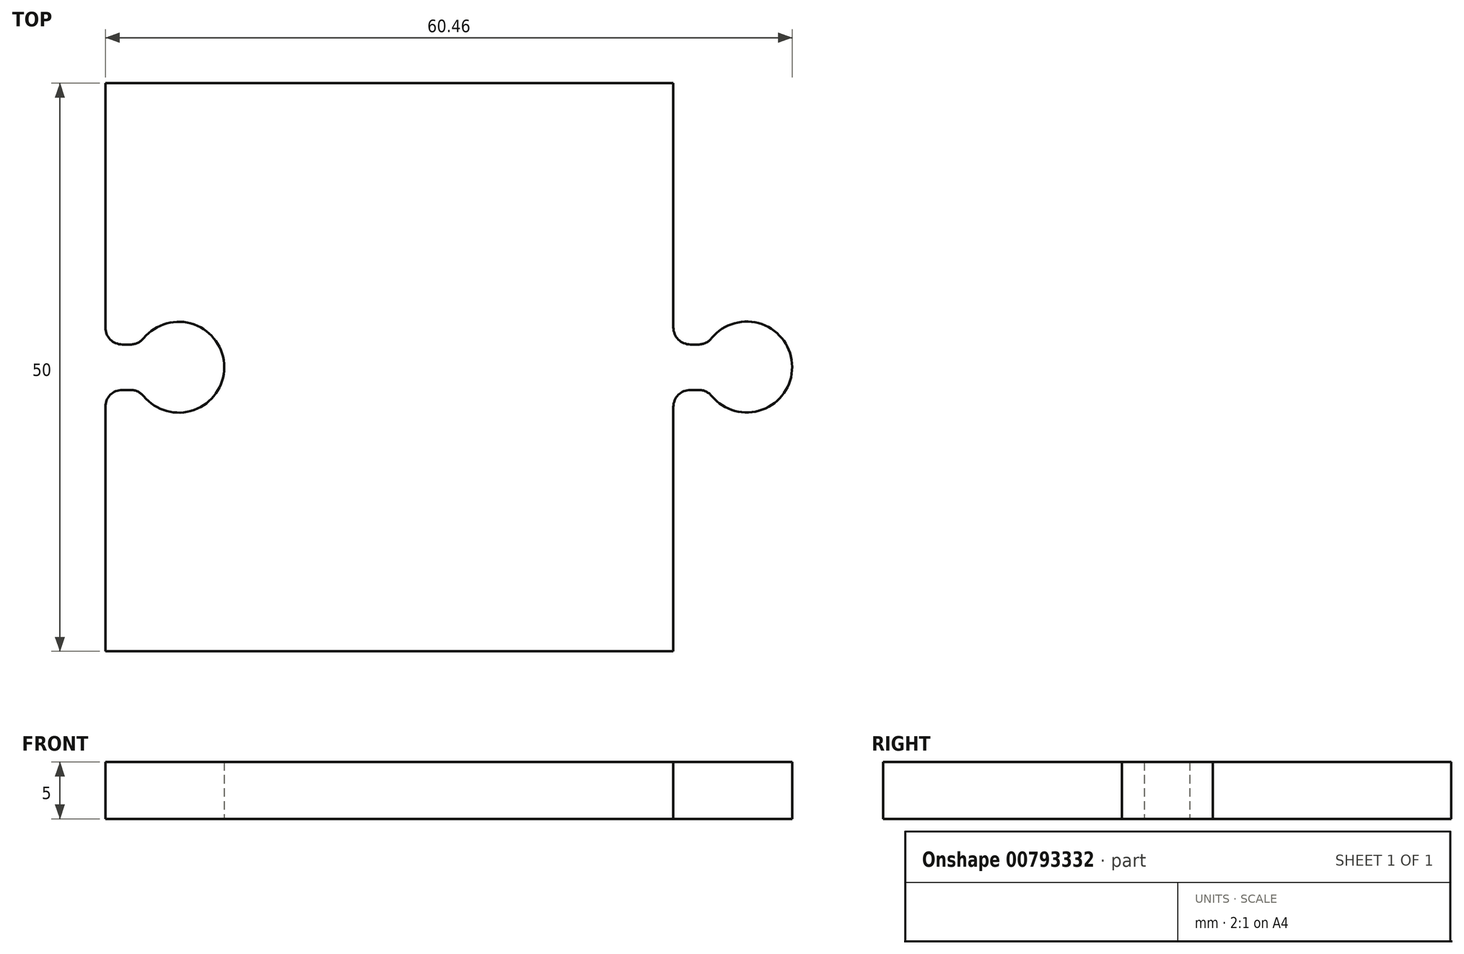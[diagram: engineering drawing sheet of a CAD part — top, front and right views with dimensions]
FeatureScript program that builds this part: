
annotation { "Feature Type Name" : "Feature", "Feature Type Description" : "" }
export const myFeature = defineFeature(function(context is Context, id is Id, definition is map)
    precondition{}
    {
        {
            var Q0;
            Q0=qCreatedBy(makeId("Top.planeOp"),FACE);
            var sketch = newSketch(context, id + "F0", { "sketchPlane" : qUnion([Q0])});
            skLineSegment(sketch, "E0.bottom", {"start": v(-26.47, 23.33) * mm, "end": v(23.53, 23.33) * mm});
            skLineSegment(sketch, "E0.top", {"start": v(-26.47, -26.67) * mm, "end": v(23.53, -26.67) * mm});
            skLineSegment(sketch, "E0.left", {"start": v(-26.47, 23.33) * mm, "end": v(-26.47, 1.83) * mm});
            skLineSegment(sketch, "E0.right", {"start": v(23.53, 23.33) * mm, "end": v(23.53, 1.83) * mm});
            skLineSegment(sketch, "E1", {"start": v(25.03, -3.67) * mm, "end": v(25.76, -3.67) * mm});
            skLineSegment(sketch, "E2", {"start": v(25.03, 0.33) * mm, "end": v(25.73, 0.33) * mm});
            skArc(sketch, "E3", {"start": v(26.91, -4.21) * mm, "mid": v(33.99, -1.64) * mm, "end": v(26.9, 0.88) * mm});
            skLineSegment(sketch, "E4.trimOffspring", {"start": v(33.46, 0.33) * mm, "end": v(33.47, 0.33) * mm});
            skLineSegment(sketch, "E5.trimOffspring", {"start": v(33.44, -3.67) * mm, "end": v(33.47, -3.67) * mm});
            skLineSegment(sketch, "E6", {"start": v(-24.97, -3.67) * mm, "end": v(-24.25, -3.67) * mm});
            skLineSegment(sketch, "E7", {"start": v(-24.97, 0.33) * mm, "end": v(-24.25, 0.33) * mm});
            skPoint(sketch, "E8.visualSharp", {"position": v(26.51, 0.33) * mm});
            skArc(sketch, "E8.filletArc", {"start": v(25.73, 0.33) * mm, "mid": v(26.37, 0.47) * mm, "end": v(26.9, 0.88) * mm});
            skPoint(sketch, "E9.visualSharp", {"position": v(26.53, -3.67) * mm});
            skArc(sketch, "E9.filletArc", {"start": v(26.91, -4.21) * mm, "mid": v(26.4, -3.81) * mm, "end": v(25.76, -3.67) * mm});
            skArc(sketch, "E10", {"start": v(-23.1, -4.22) * mm, "mid": v(-16.01, -1.67) * mm, "end": v(-23.1, 0.88) * mm});
            skPoint(sketch, "E11", {"position": v(23.53, -1.65) * mm});
            skLineSegment(sketch, "E12.trimOffspring", {"start": v(23.53, -5.17) * mm, "end": v(23.53, -26.67) * mm});
            skLineSegment(sketch, "E13.trimOffspring", {"start": v(-26.47, -5.17) * mm, "end": v(-26.47, -26.67) * mm});
            skPoint(sketch, "E14.visualSharp", {"position": v(-23.48, 0.33) * mm});
            skArc(sketch, "E14.filletArc", {"start": v(-24.25, 0.33) * mm, "mid": v(-23.61, 0.47) * mm, "end": v(-23.1, 0.88) * mm});
            skPoint(sketch, "E15.visualSharp", {"position": v(-23.48, -3.67) * mm});
            skArc(sketch, "E15.filletArc", {"start": v(-23.1, -4.22) * mm, "mid": v(-23.61, -3.81) * mm, "end": v(-24.25, -3.67) * mm});
            skPoint(sketch, "E16.visualSharp", {"position": v(23.53, 0.33) * mm});
            skArc(sketch, "E16.filletArc", {"start": v(23.53, 1.83) * mm, "mid": v(23.97, 0.77) * mm, "end": v(25.03, 0.33) * mm});
            skPoint(sketch, "E17.visualSharp", {"position": v(23.53, -3.67) * mm});
            skArc(sketch, "E17.filletArc", {"start": v(25.03, -3.67) * mm, "mid": v(23.97, -4.1) * mm, "end": v(23.53, -5.17) * mm});
            skPoint(sketch, "E18.visualSharp", {"position": v(-26.47, 0.33) * mm});
            skArc(sketch, "E18.filletArc", {"start": v(-26.47, 1.83) * mm, "mid": v(-26.03, 0.77) * mm, "end": v(-24.97, 0.33) * mm});
            skPoint(sketch, "E19.visualSharp", {"position": v(-26.47, -3.67) * mm});
            skArc(sketch, "E19.filletArc", {"start": v(-24.97, -3.67) * mm, "mid": v(-26.03, -4.1) * mm, "end": v(-26.47, -5.17) * mm});
            skSolve(sketch);
        }
        {
            var Q0;
            Q0 = qSketchRegion(id + "F0", true);
            extrude(context, id + "F1", {"entities" : qUnion([Q0]), "depth" : 5 * mm, "offsetDistance" : 25 * mm});
        }
    });
